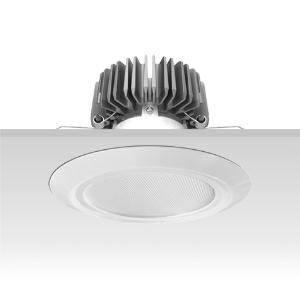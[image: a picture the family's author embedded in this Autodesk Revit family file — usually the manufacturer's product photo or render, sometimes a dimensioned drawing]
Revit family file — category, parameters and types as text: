
# Revit family: 3f_filippi_-_3f_reno_bianco_ampio_3f_filippi_-_30641_a01048_-_3f_reno_200_wh_4000-930_wide___smp_wh_5f31
name_source: partatom
category: Lighting Fixtures
units: mm (PartAtom-declared; Revit-internal decimal feet)

## family parameters
Cut with Voids When Loaded = No
Host = Face
Light Source = No
Part Type = Normal
Room Calculation Point = No
Round Connector Dimension = Use Diameter
Shared = No

## types (1)
- 3F Filippi - 3F Reno Bianco Ampio (1 x LED, 2801 lm, 43 W, 3000 K)
    Apparent Load = 43 VA
    Approval mark = CE
    CIE Flux Codes = 74 92 98 100 100
    Color Rendering = 90
    Color Temperature = 3000 K
    Control Gear = Electronic ballast
    Default Elevation = 1800 mm
    Description = ILLUMINOTECHNICAL
Luminous efficiency 100% (DLOR 100%, ULOR 0%).
Initial luminous flux of the luminaire 2801 lm.
Direct symmetric wide distribution.
Installation Interdistance Transv.D = 1.06 x hu - Long.D = 1.04 x hu.
Tabular UGR (CIE 117 - 4H-8H; S=0.25H; 70/50/20): RUG 23.1 - 23.
Beam angle: 70° - 69°.
Luminous efficacy 65 lm/W.
Lifetime (L90/B10): 30000 h. (tq+25°C)
Lifetime (L85/B10): 50000 h. (tq+25°C)
Lifetime (L70/B10): 80000 h. (tq+25°C)
Sudden decreased luminous flux after 50000 hours: 0% (C0).
Photobiological safety in compliance with IEC/TR 62778: RG1 low risk, (IEC 62471).
In compliance with IEC/EN 62722-2-1 - IEC/EN 62717 standards.

SOURCE
Compact LED module 4000/930.
Energy efficiency class (UE 2019/2020 - UE 2019/2015): F.
CIE 13.3 Colour rendering index: CRI >90 (R9 >50%).
IES TM-30 Fidelity Index: Rf = 92 Rg = 101.
CCT nominal colour temperature 3000 K.
Colour initial tolerance (MacAdam): SDCM 3.
Zhaga Book 3 compliant.

MECHANICAL
Passive heat dissipator in die-casting aluminium, oversized, for optimum thermal management of the LED module.
Parabolic element with graduated/concentric rings in white polycarbonate.
Transparent external lens with glossy and satin differentiated surfaces, with a cooling and anti-insect system in methacrylate (PMMA).
Fastening spring clips in stainless steel.
Dimensions: diameter 226 mm, height 146 mm. Weight 1.645 kg.
IP44 protection degree for exposed part, IP20 for recessed part.
Mechanical strength to impacts IK05 (0.7 joule).
Glow-wire test resistance 650°C.

ELECTRICAL
Wiring on a separate unit.
Halogen Free electronic wiring 230V-50/60Hz, power factor 0.95, THD <25%, constant output current, SELV, class II, 1 driver.
Power of the luminaire 43 W.
ENEC - CE.
SAFE FLICKER: PstLM=<1 and SVM=<0.4 (IEC TR 61547-1 and IEC TR 63158), to ensure a more comfortable and safe light.
Luminaire compliant with EN 60598-2-22 for power supply from a centralised emergency system CPSS (Central Power Supply System), not incorporated in the luminaire - high risk areas excluded. The default power and flux are 100% in AC and 100% in DC.
Ambient temperature from 0°C to +25°C.
Temperature class T6 max 85°C.
Relative humidity UR: <85%.

INSTALLATION
Pull-up recessed fitting.
False ceiling carving: 200 mm.
All accessories dedicated to this product are available on the Catalog and on our website www.3F-Filippi.com.

ACCESSORIES
A01048 - Anti-glare microprismatic SMP diffuser in methacrylate (PMMA), locked and in line with the trim, in white polycarbonate.

APPLICATIONS
Suitable product for food production plants (HACCP), IFS (Food Version 6), BRC (GSFS Food Version 7).
Environments: architectural, commercial, exhibition areas, transit areas, corridors, shops, display windows, service areas.
In false ceilings with narrow voids.

WARNING
Luminaire designed for disposal/recycling at end-of-life.
Replaceable (LED only) light source by a professional. Replaceable control gear by a professional.
    Height = 0 mm  [stored 0 ft]
    Lamp = 1 x LED
    Lamp Light Flux = 2801 lm
    Lamp Power = 43 W
    Lamp count = 1
    Length = 226 mm
    Lifetime = 50000 h
    Luminous efficacy = 65 lm/W
    Manufacturer = 3F Filippi
    ModVariant = No
    Model = 3F Filippi - 30641+A01048 - 3F Reno 200 WH 4000-930 WIDE + SMP WH
    Mounting Place = Ceiling
    Mounting Type = Recessed
    Number of Poles = 1
    OnlyDefault = Yes
    Power Factor = 1
    Product Name = 3F Filippi - 3F Reno Bianco Ampio
    Product group = recessed luminaire
    ProductGroupID = 4
    Protection Class = Protection class II
    Protection Degree = IP 20
    RLX_Detail_Level = 1
    RLX_Emergency_Light_Flux = 0 lm
    RLX_Emergency_Type = 0
    RLX_Emergency_Type_DB = No
    RlxData = <blob elided: 94465 chars, md5=01853052>
    Socket = socket
    Standby Power = 0 W
    System Light Flux = 2801 lm
    System Power = 43 W
    Type Comments = Product without accessories
    Type Image = 3ffilippi_3f_reno_200_wh_vs_smp.jpg
    URL = http://relux.com
    VarID = ---
    Voltage = 0 V
    Weight = 0.00 kg
    Width = 0 mm  [stored 0 ft]

note: [stored X ft] marks values corroborated as IEEE doubles in the binary element streams (Revit-internal decimal feet)

## geometry (parser evidence)
native form markers: Blend x4, Sweep x10
no freeform markers — native parametric forms only
